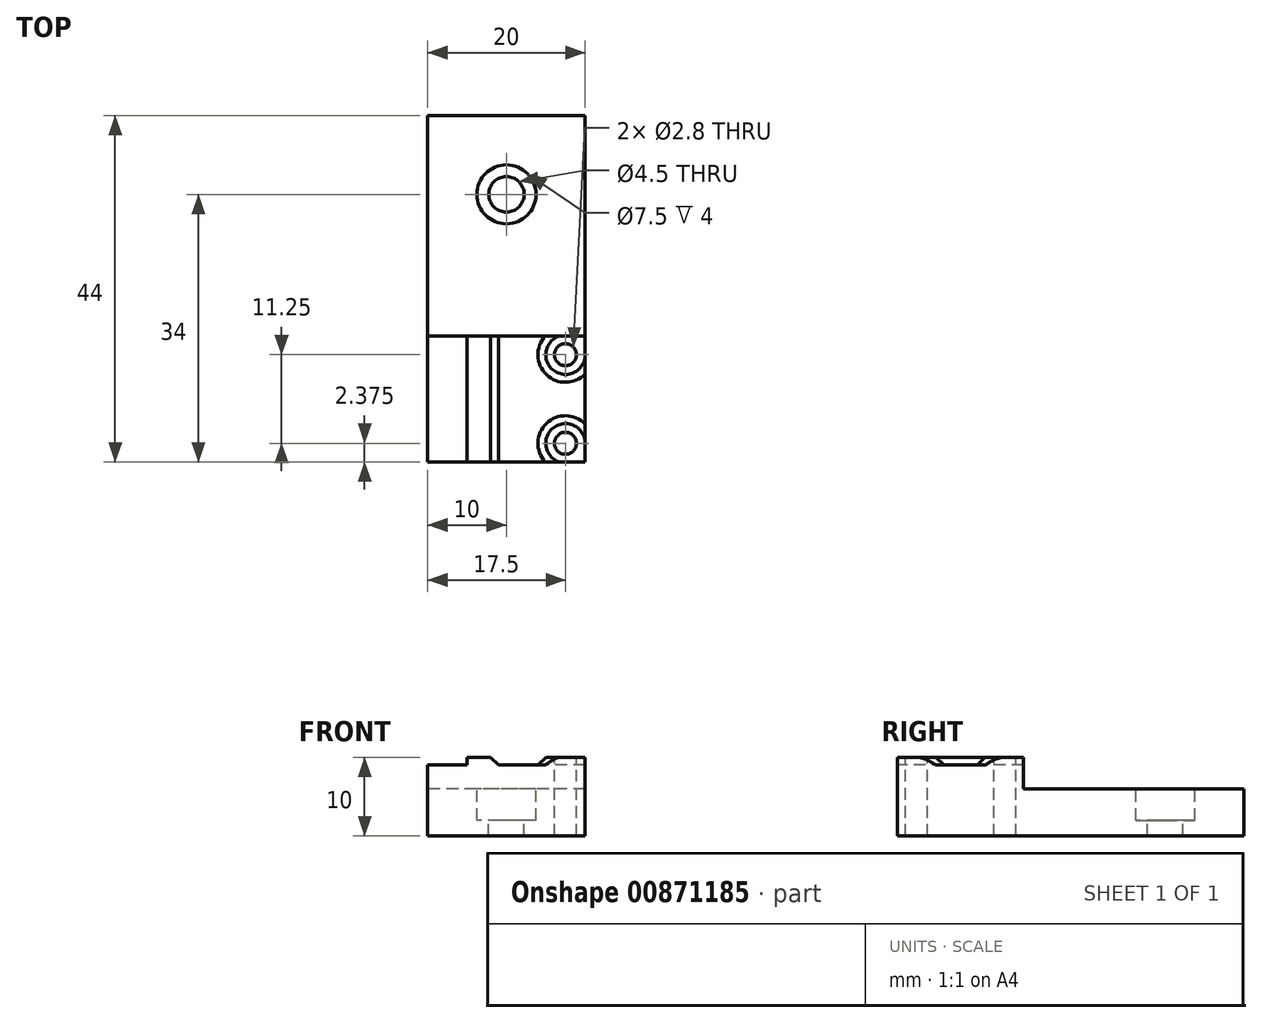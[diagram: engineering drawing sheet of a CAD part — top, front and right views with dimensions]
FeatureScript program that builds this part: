
annotation { "Feature Type Name" : "Feature", "Feature Type Description" : "" }
export const myFeature = defineFeature(function(context is Context, id is Id, definition is map)
    precondition{}
    {
        {
            var Q0;
            Q0=qCreatedBy(makeId("Top.planeOp"),FACE);
            var sketch = newSketch(context, id + "F0", { "sketchPlane" : qUnion([Q0])});
            skLineSegment(sketch, "E0.bottom", {"start": v(10, -22) * mm, "end": v(-10, -22) * mm});
            skLineSegment(sketch, "E0.top", {"start": v(10, 22) * mm, "end": v(-10, 22) * mm});
            skLineSegment(sketch, "E0.left", {"start": v(10, -22) * mm, "end": v(10, 22) * mm});
            skLineSegment(sketch, "E0.right", {"start": v(-10, -22) * mm, "end": v(-10, 22) * mm});
            skPoint(sketch, "E0.middle", {"position": v(0, 0) * mm});
            skSolve(sketch);
        }
        {
            var Q0;
            Q0 = qSketchRegion(id + "F0", true);
            extrude(context, id + "F1", {"entities" : qUnion([Q0]), "depth" : 10 * mm, "offsetDistance" : 25 * mm});
        }
        {
            var Q0;
            Q0=makeQuery(id+"F1.opExtrude","CAP_FACE",FACE,{"disambiguationData":[OSD([sQuery(id+"F0.wireOp",EDGE,"E0.bottom"),sQuery(id+"F0.wireOp",EDGE,"E0.top"),sQuery(id+"F0.wireOp",EDGE,"E0.left"),sQuery(id+"F0.wireOp",EDGE,"E0.right")])],"isStart":false});
            var sketch = newSketch(context, id + "F2", { "sketchPlane" : qUnion([Q0])});
            skCircle(sketch, "E1", {"center": v(7.5, -19.62) * mm, "radius": 1.4 * mm});
            skCircle(sketch, "E2", {"center": v(7.5, -8.38) * mm, "radius": 1.4 * mm});
            skSolve(sketch);
        }
        {
            var Q0;
            Q0=makeQuery(id+"F2.imprint","IMPRINT",FACE,{"disambiguationData":[TD([[makeQuery(id+"F2.imprint","IMPRINT",EDGE,{"derivedFrom":sQuery(id+"F2.wireOp",EDGE,"E1")}),1.0]])]});
            var Q1;
            Q1=makeQuery(id+"F2.imprint","IMPRINT",FACE,{"disambiguationData":[TD([[makeQuery(id+"F2.imprint","IMPRINT",EDGE,{"derivedFrom":sQuery(id+"F2.wireOp",EDGE,"E2")}),1.0]])]});
            extrude(context, id + "F3", {"entities" : qUnion([Q0, Q1]), "operationType" : NewBodyOperationType.REMOVE, "endBound" : BoundingType.THROUGH_ALL, "oppositeDirection" : true, "depth" : 25 * mm, "offsetDistance" : 25 * mm});
        }
        {
            var Q0;
            Q0=makeQuery(id+"F1.opExtrude","SWEPT_FACE",FACE,{"disambiguationData":[OSD([sQuery(id+"F0.wireOp",EDGE,"E0.right")])]});
            var sketch = newSketch(context, id + "F4", { "sketchPlane" : qUnion([Q0])});
            skLineSegment(sketch, "E3", {"start": v(22, 9) * mm, "end": v(6, 9) * mm});
            skLineSegment(sketch, "E4", {"start": v(6, 9) * mm, "end": v(6, 6) * mm});
            skLineSegment(sketch, "E5", {"start": v(6, 6) * mm, "end": v(-22, 6) * mm});
            skSolve(sketch);
        }
        {
            var Q0;
            {var subQ3=sQuery(id+"F4.wireOp",EDGE,"E3");Q0=makeQuery(id+"F4.imprint","IMPRINT",FACE,{"disambiguationData":[TD([[makeQuery(id+"F4.imprint","IMPRINT",EDGE,{"derivedFrom":subQ3}),-1.0]])]});}
            extrude(context, id + "F5", {"entities" : qUnion([Q0]), "operationType" : NewBodyOperationType.REMOVE, "endBound" : BoundingType.THROUGH_ALL, "oppositeDirection" : true, "depth" : 25 * mm, "offsetDistance" : 25 * mm});
        }
        {
            var Q0;
            Q0=makeQuery(id+"F5.boolean.opBoolean","COPY",FACE,{"derivedFrom":makeQuery(id+"F5.opExtrude","SWEPT_FACE",FACE,{"disambiguationData":[OSD([sQuery(id+"F4.wireOp",EDGE,"E5")])]})});
            var sketch = newSketch(context, id + "F6", { "sketchPlane" : qUnion([Q0])});
            skCircle(sketch, "E6", {"center": v(0, 12) * mm, "radius": 2.25 * mm});
            skSolve(sketch);
        }
        {
            var Q0;
            Q0 = qSketchRegion(id + "F6", true);
            extrude(context, id + "F7", {"entities" : qUnion([Q0]), "operationType" : NewBodyOperationType.REMOVE, "endBound" : BoundingType.THROUGH_ALL, "oppositeDirection" : true, "depth" : 25 * mm, "offsetDistance" : 25 * mm});
        }
        {
            var Q0;
            Q0=makeQuery(id+"F5.boolean.opBoolean","COPY",FACE,{"derivedFrom":makeQuery(id+"F5.opExtrude","SWEPT_FACE",FACE,{"disambiguationData":[OSD([sQuery(id+"F4.wireOp",EDGE,"E5")])]})});
            var sketch = newSketch(context, id + "F8", { "sketchPlane" : qUnion([Q0])});
            skCircle(sketch, "E7", {"center": v(0, 12) * mm, "radius": 3.75 * mm});
            skSolve(sketch);
        }
        {
            var Q0;
            Q0 = qSketchRegion(id + "F8", true);
            extrude(context, id + "F9", {"entities" : qUnion([Q0]), "operationType" : NewBodyOperationType.REMOVE, "oppositeDirection" : true, "depth" : 4 * mm, "offsetDistance" : 25 * mm});
        }
        {
            var Q0;
            Q0=makeQuery(id+"F5.boolean.opBoolean","COPY",FACE,{"derivedFrom":makeQuery(id+"F5.opExtrude","SWEPT_FACE",FACE,{"disambiguationData":[OSD([sQuery(id+"F4.wireOp",EDGE,"E3")])]})});
            var sketch = newSketch(context, id + "F10", { "sketchPlane" : qUnion([Q0])});
            skCircle(sketch, "E8", {"center": v(7.5, -8.37) * mm, "radius": 3.5 * mm});
            skCircle(sketch, "E9", {"center": v(7.5, -19.62) * mm, "radius": 3.5 * mm});
            skLineSegment(sketch, "E10.bottom", {"start": v(-5, -6) * mm, "end": v(-2, -6) * mm});
            skLineSegment(sketch, "E10.top", {"start": v(-5, -22) * mm, "end": v(-2, -22) * mm});
            skLineSegment(sketch, "E10.left", {"start": v(-5, -6) * mm, "end": v(-5, -22) * mm});
            skLineSegment(sketch, "E10.right", {"start": v(-2, -6) * mm, "end": v(-2, -22) * mm});
            skSolve(sketch);
        }
        {
            var Q0;
            Q0=makeQuery(id+"F10.imprint","IMPRINT",FACE,{"disambiguationData":[TD([[makeQuery(id+"F10.imprint","IMPRINT",EDGE,{"derivedFrom":sQuery(id+"F10.wireOp",EDGE,"E10.bottom")}),1.0]])]});
            var Q1;
            {var subQ1=sQuery(id+"F4.wireOp",EDGE,"E3");Q1=makeQuery(id+"F10.imprint","IMPRINT",FACE,{"disambiguationData":[TD([[makeQuery(id+"F10.imprint","IMPRINT",EDGE,{"derivedFrom":makeQuery(id+"F5.boolean.opBoolean","INTERSECT",EDGE,{"derivedFrom":[makeQuery(id+"F3.boolean.opBoolean","COPY",FACE,{"derivedFrom":makeQuery(id+"F3.opExtrude","SWEPT_FACE",FACE,{"disambiguationData":[OSD([sQuery(id+"F2.wireOp",EDGE,"E2")])]})}),makeQuery(id+"F5.opExtrude","SWEPT_FACE",FACE,{"disambiguationData":[OSD([subQ1])]})]})}),1.0]])]});}
            var Q2;
            {var subQ1=sQuery(id+"F4.wireOp",EDGE,"E3");Q2=makeQuery(id+"F10.imprint","IMPRINT",FACE,{"disambiguationData":[TD([[makeQuery(id+"F10.imprint","IMPRINT",EDGE,{"derivedFrom":makeQuery(id+"F5.boolean.opBoolean","INTERSECT",EDGE,{"derivedFrom":[makeQuery(id+"F3.boolean.opBoolean","COPY",FACE,{"derivedFrom":makeQuery(id+"F3.opExtrude","SWEPT_FACE",FACE,{"disambiguationData":[OSD([sQuery(id+"F2.wireOp",EDGE,"E1")])]})}),makeQuery(id+"F5.opExtrude","SWEPT_FACE",FACE,{"disambiguationData":[OSD([subQ1])]})]})}),1.0]])]});}
            extrude(context, id + "F11", {"entities" : qUnion([Q0, Q1, Q2]), "operationType" : NewBodyOperationType.ADD, "depth" : 1 * mm, "offsetDistance" : 25 * mm});
        }
        {
            var Q0;
            Q0=makeQuery(id+"F11.opExtrude","CAP_EDGE",EDGE,{"disambiguationData":[OSD([sQuery(id+"F10.wireOp",EDGE,"E8")])],"isStart":false});
            var Q1;
            Q1=makeQuery(id+"F11.opExtrude","CAP_EDGE",EDGE,{"disambiguationData":[OSD([sQuery(id+"F10.wireOp",EDGE,"E9")])],"isStart":false});
            var Q2;
            Q2=makeQuery(id+"F11.opExtrude","CAP_EDGE",EDGE,{"disambiguationData":[OSD([sQuery(id+"F10.wireOp",EDGE,"E10.left")])],"isStart":true});
            var Q3;
            Q3=makeQuery(id+"F11.opExtrude","CAP_EDGE",EDGE,{"disambiguationData":[OSD([sQuery(id+"F10.wireOp",EDGE,"E10.right")])],"isStart":true});
            chamfer(context, id + "F12", {"entities" : qUnion([Q0, Q1, Q2, Q3]), "width" : 1 * mm, "tangentPropagation" : true});
        }
    });
